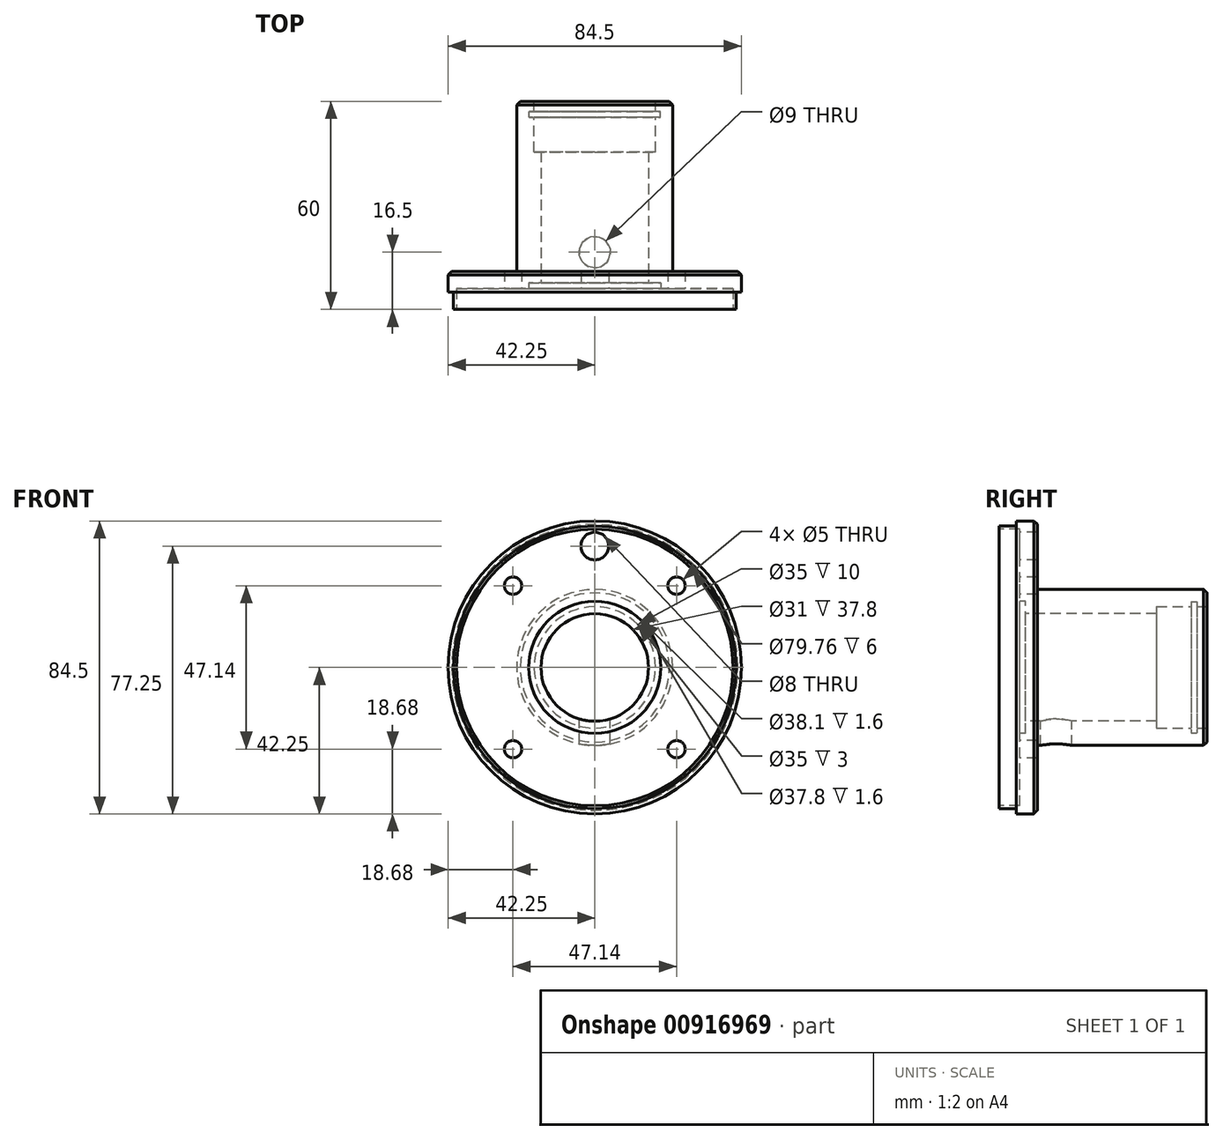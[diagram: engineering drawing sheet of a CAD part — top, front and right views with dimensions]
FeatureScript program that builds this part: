
annotation { "Feature Type Name" : "Feature", "Feature Type Description" : "" }
export const myFeature = defineFeature(function(context is Context, id is Id, definition is map)
    precondition{}
    {
        {
            var Q0;
            Q0=qCreatedBy(makeId("Front.planeOp"),FACE);
            var sketch = newSketch(context, id + "F0", { "sketchPlane" : qUnion([Q0])});
            skCircle(sketch, "E0", {"center": v(0, 0) * mm, "radius": 42.25 * mm});
            skSolve(sketch);
        }
        {
            var Q0;
            Q0 = qSketchRegion(id + "F0", true);
            extrude(context, id + "F1", {"entities" : qUnion([Q0]), "depth" : 11 * mm, "offsetDistance" : 25 * mm});
        }
        {
            var Q0;
            Q0=makeQuery(id+"F1.opExtrude","CAP_FACE",FACE,{"disambiguationData":[OSD([sQuery(id+"F0.wireOp",EDGE,"E0")])],"isStart":false});
            var sketch = newSketch(context, id + "F2", { "sketchPlane" : qUnion([Q0])});
            skCircle(sketch, "E1", {"center": v(0, 0) * mm, "radius": 40.75 * mm});
            skSolve(sketch);
        }
        {
            var Q0;
            Q0=makeQuery(id+"F2.imprint","IMPRINT",FACE,{"disambiguationData":[TD([[makeQuery(id+"F2.imprint","IMPRINT",EDGE,{"derivedFrom":sQuery(id+"F2.wireOp",EDGE,"E1")}),-1.0]])]});
            extrude(context, id + "F3", {"entities" : qUnion([Q0]), "operationType" : NewBodyOperationType.REMOVE, "oppositeDirection" : true, "depth" : 5 * mm, "offsetDistance" : 25 * mm});
        }
        {
            var Q0;
            Q0=makeQuery(id+"F1.opExtrude","CAP_FACE",FACE,{"disambiguationData":[OSD([sQuery(id+"F0.wireOp",EDGE,"E0")])],"isStart":false});
            var sketch = newSketch(context, id + "F4", { "sketchPlane" : qUnion([Q0])});
            skCircle(sketch, "E2", {"center": v(0, 0) * mm, "radius": 39.88 * mm});
            skSolve(sketch);
        }
        {
            var Q0;
            Q0 = qSketchRegion(id + "F4", true);
            extrude(context, id + "F5", {"entities" : qUnion([Q0]), "operationType" : NewBodyOperationType.REMOVE, "oppositeDirection" : true, "depth" : 6 * mm, "offsetDistance" : 25 * mm});
        }
        {
            var Q0;
            Q0=makeQuery(id+"F5.boolean.opBoolean","COPY",FACE,{"derivedFrom":makeQuery(id+"F5.opExtrude","CAP_FACE",FACE,{"disambiguationData":[OSD([sQuery(id+"F4.wireOp",EDGE,"E2")])],"isStart":false})});
            var sketch = newSketch(context, id + "F6", { "sketchPlane" : qUnion([Q0])});
            skLineSegment(sketch, "E3.bottom", {"start": v(-23.57, -23.57) * mm, "end": v(23.57, -23.57) * mm, "construction": true});
            skLineSegment(sketch, "E3.top", {"start": v(-23.57, 23.57) * mm, "end": v(23.57, 23.57) * mm, "construction": true});
            skLineSegment(sketch, "E3.left", {"start": v(-23.57, -23.57) * mm, "end": v(-23.57, 23.57) * mm, "construction": true});
            skLineSegment(sketch, "E3.right", {"start": v(23.57, -23.57) * mm, "end": v(23.57, 23.57) * mm, "construction": true});
            skCircle(sketch, "E4", {"center": v(-23.57, 23.57) * mm, "radius": 2.5 * mm});
            skCircle(sketch, "E5", {"center": v(23.57, 23.57) * mm, "radius": 2.5 * mm});
            skCircle(sketch, "E6", {"center": v(23.57, -23.57) * mm, "radius": 2.5 * mm});
            skCircle(sketch, "E7", {"center": v(-23.57, -23.57) * mm, "radius": 2.5 * mm});
            skCircle(sketch, "E8", {"center": v(0, 35) * mm, "radius": 4 * mm});
            skPoint(sketch, "E8.centerSnap0", {"position": v(0, 23.57) * mm});
            skSolve(sketch);
        }
        {
            var Q0;
            Q0=makeQuery(id+"F6.imprint","IMPRINT",FACE,{"disambiguationData":[TD([[makeQuery(id+"F6.imprint","IMPRINT",EDGE,{"derivedFrom":sQuery(id+"F6.wireOp",EDGE,"E4")}),1.0]])]});
            var Q1;
            Q1=makeQuery(id+"F6.imprint","IMPRINT",FACE,{"disambiguationData":[TD([[makeQuery(id+"F6.imprint","IMPRINT",EDGE,{"derivedFrom":sQuery(id+"F6.wireOp",EDGE,"E5")}),1.0]])]});
            var Q2;
            Q2=makeQuery(id+"F6.imprint","IMPRINT",FACE,{"disambiguationData":[TD([[makeQuery(id+"F6.imprint","IMPRINT",EDGE,{"derivedFrom":sQuery(id+"F6.wireOp",EDGE,"E6")}),1.0]])]});
            var Q3;
            Q3=makeQuery(id+"F6.imprint","IMPRINT",FACE,{"disambiguationData":[TD([[makeQuery(id+"F6.imprint","IMPRINT",EDGE,{"derivedFrom":sQuery(id+"F6.wireOp",EDGE,"E7")}),1.0]])]});
            var Q4;
            Q4=makeQuery(id+"F6.imprint","IMPRINT",FACE,{"disambiguationData":[TD([[makeQuery(id+"F6.imprint","IMPRINT",EDGE,{"derivedFrom":sQuery(id+"F6.wireOp",EDGE,"E8")}),1.0]])]});
            extrude(context, id + "F7", {"entities" : qUnion([Q0, Q1, Q2, Q3, Q4]), "operationType" : NewBodyOperationType.REMOVE, "endBound" : BoundingType.THROUGH_ALL, "oppositeDirection" : true, "depth" : 25 * mm, "offsetDistance" : 25 * mm});
        }
        {
            var Q0;
            Q0=makeQuery(id+"F5.boolean.opBoolean","COPY",FACE,{"derivedFrom":makeQuery(id+"F5.opExtrude","CAP_FACE",FACE,{"disambiguationData":[OSD([sQuery(id+"F4.wireOp",EDGE,"E2")])],"isStart":false})});
            var sketch = newSketch(context, id + "F8", { "sketchPlane" : qUnion([Q0])});
            skCircle(sketch, "E9", {"center": v(0, 0) * mm, "radius": 19.05 * mm});
            skSolve(sketch);
        }
        {
            var Q0;
            Q0=makeQuery(id+"F8.imprint","IMPRINT",FACE,{"disambiguationData":[TD([[makeQuery(id+"F8.imprint","IMPRINT",EDGE,{"derivedFrom":sQuery(id+"F8.wireOp",EDGE,"E9")}),1.0]])]});
            extrude(context, id + "F9", {"entities" : qUnion([Q0]), "operationType" : NewBodyOperationType.REMOVE, "oppositeDirection" : true, "depth" : 1.6 * mm, "offsetDistance" : 25 * mm});
        }
        {
            var Q0;
            Q0=makeQuery(id+"F1.opExtrude","CAP_FACE",FACE,{"disambiguationData":[OSD([sQuery(id+"F0.wireOp",EDGE,"E0")])],"isStart":true});
            var sketch = newSketch(context, id + "F10", { "sketchPlane" : qUnion([Q0])});
            skCircle(sketch, "E10", {"center": v(0, 0) * mm, "radius": 22.5 * mm});
            skSolve(sketch);
        }
        {
            var Q0;
            Q0=makeQuery(id+"F10.imprint","IMPRINT",FACE,{"disambiguationData":[TD([[makeQuery(id+"F10.imprint","IMPRINT",EDGE,{"derivedFrom":sQuery(id+"F10.wireOp",EDGE,"E10")}),1.0]])]});
            extrude(context, id + "F11", {"entities" : qUnion([Q0]), "operationType" : NewBodyOperationType.ADD, "depth" : 49 * mm, "offsetDistance" : 25 * mm});
        }
        {
            var Q0;
            Q0=makeQuery(id+"F9.boolean.opBoolean","COPY",FACE,{"derivedFrom":makeQuery(id+"F9.opExtrude","CAP_FACE",FACE,{"disambiguationData":[OSD([sQuery(id+"F8.wireOp",EDGE,"E9")])],"isStart":false})});
            var sketch = newSketch(context, id + "F12", { "sketchPlane" : qUnion([Q0])});
            skCircle(sketch, "E11", {"center": v(0, 0) * mm, "radius": 15.5 * mm});
            skSolve(sketch);
        }
        {
            var Q0;
            Q0=makeQuery(id+"F12.imprint","IMPRINT",FACE,{"disambiguationData":[TD([[makeQuery(id+"F12.imprint","IMPRINT",EDGE,{"derivedFrom":sQuery(id+"F12.wireOp",EDGE,"E11")}),1.0]])]});
            extrude(context, id + "F13", {"entities" : qUnion([Q0]), "operationType" : NewBodyOperationType.REMOVE, "endBound" : BoundingType.THROUGH_ALL, "oppositeDirection" : true, "depth" : 25 * mm, "offsetDistance" : 25 * mm});
        }
        {
            var Q0;
            Q0=makeQuery(id+"F11.opExtrude","CAP_FACE",FACE,{"disambiguationData":[OSD([sQuery(id+"F10.wireOp",EDGE,"E10")])],"isStart":false});
            var sketch = newSketch(context, id + "F14", { "sketchPlane" : qUnion([Q0])});
            skCircle(sketch, "E12", {"center": v(0, 0) * mm, "radius": 17.5 * mm});
            skSolve(sketch);
        }
        {
            var Q0;
            Q0=makeQuery(id+"F14.imprint","IMPRINT",FACE,{"disambiguationData":[TD([[makeQuery(id+"F14.imprint","IMPRINT",EDGE,{"derivedFrom":sQuery(id+"F14.wireOp",EDGE,"E12")}),1.0]])]});
            extrude(context, id + "F15", {"entities" : qUnion([Q0]), "operationType" : NewBodyOperationType.REMOVE, "oppositeDirection" : true, "depth" : 14.6 * mm, "offsetDistance" : 25 * mm});
        }
        {
            var Q0;
            Q0=makeQuery(id+"F11.opExtrude","CAP_FACE",FACE,{"disambiguationData":[OSD([sQuery(id+"F10.wireOp",EDGE,"E10")])],"isStart":false});
            cPlane(context, id + "F16", {"entities" : qUnion([Q0]), "cplaneType" : CPlaneType.OFFSET, "offset" : 3 * mm, "oppositeDirection" : true, "width" : 150 * mm, "height" : 150 * mm});
        }
        {
            var Q0;
            Q0=qCreatedBy(id+"F16.planeOp",FACE);
            var sketch = newSketch(context, id + "F17", { "sketchPlane" : qUnion([Q0])});
            skCircle(sketch, "E13", {"center": v(0, 0) * mm, "radius": 18.9 * mm});
            skSolve(sketch);
        }
        {
            var Q0;
            Q0 = qSketchRegion(id + "F17", true);
            extrude(context, id + "F18", {"entities" : qUnion([Q0]), "operationType" : NewBodyOperationType.REMOVE, "oppositeDirection" : true, "depth" : 1.6 * mm, "offsetDistance" : 25 * mm});
        }
        {
            var Q0;
            Q0=makeQuery(id+"F11.opExtrude","CAP_EDGE",EDGE,{"disambiguationData":[OSD([sQuery(id+"F10.wireOp",EDGE,"E10")])],"isStart":false});
            var Q1;
            Q1=makeQuery(id+"F15.boolean.opBoolean","COPY",EDGE,{"derivedFrom":makeQuery(id+"F15.opExtrude","CAP_EDGE",EDGE,{"disambiguationData":[OSD([sQuery(id+"F14.wireOp",EDGE,"E12")])],"isStart":true})});
            var Q2;
            Q2=makeQuery(id+"F1.opExtrude","CAP_EDGE",EDGE,{"disambiguationData":[OSD([sQuery(id+"F0.wireOp",EDGE,"E0")])],"isStart":true});
            var Q3;
            Q3=makeQuery(id+"F3.boolean.opBoolean","COPY",EDGE,{"derivedFrom":makeQuery(id+"F3.opExtrude","CAP_EDGE",EDGE,{"disambiguationData":[OSD([sQuery(id+"F0.wireOp",EDGE,"E0")])],"isStart":false})});
            chamfer(context, id + "F19", {"entities" : qUnion([Q0, Q1, Q2, Q3]), "width" : 1 * mm, "tangentPropagation" : true});
        }
        {
            var Q0;
            Q0=qCreatedBy(makeId("Top.planeOp"),FACE);
            var sketch = newSketch(context, id + "F20", { "sketchPlane" : qUnion([Q0])});
            skCircle(sketch, "E14", {"center": v(0, 5.5) * mm, "radius": 4.5 * mm});
            skSolve(sketch);
        }
        {
            var Q0;
            Q0 = qSketchRegion(id + "F20", true);
            extrude(context, id + "F21", {"entities" : qUnion([Q0]), "operationType" : NewBodyOperationType.REMOVE, "endBound" : BoundingType.THROUGH_ALL, "oppositeDirection" : true, "depth" : 25 * mm, "offsetDistance" : 25 * mm});
        }
    });
